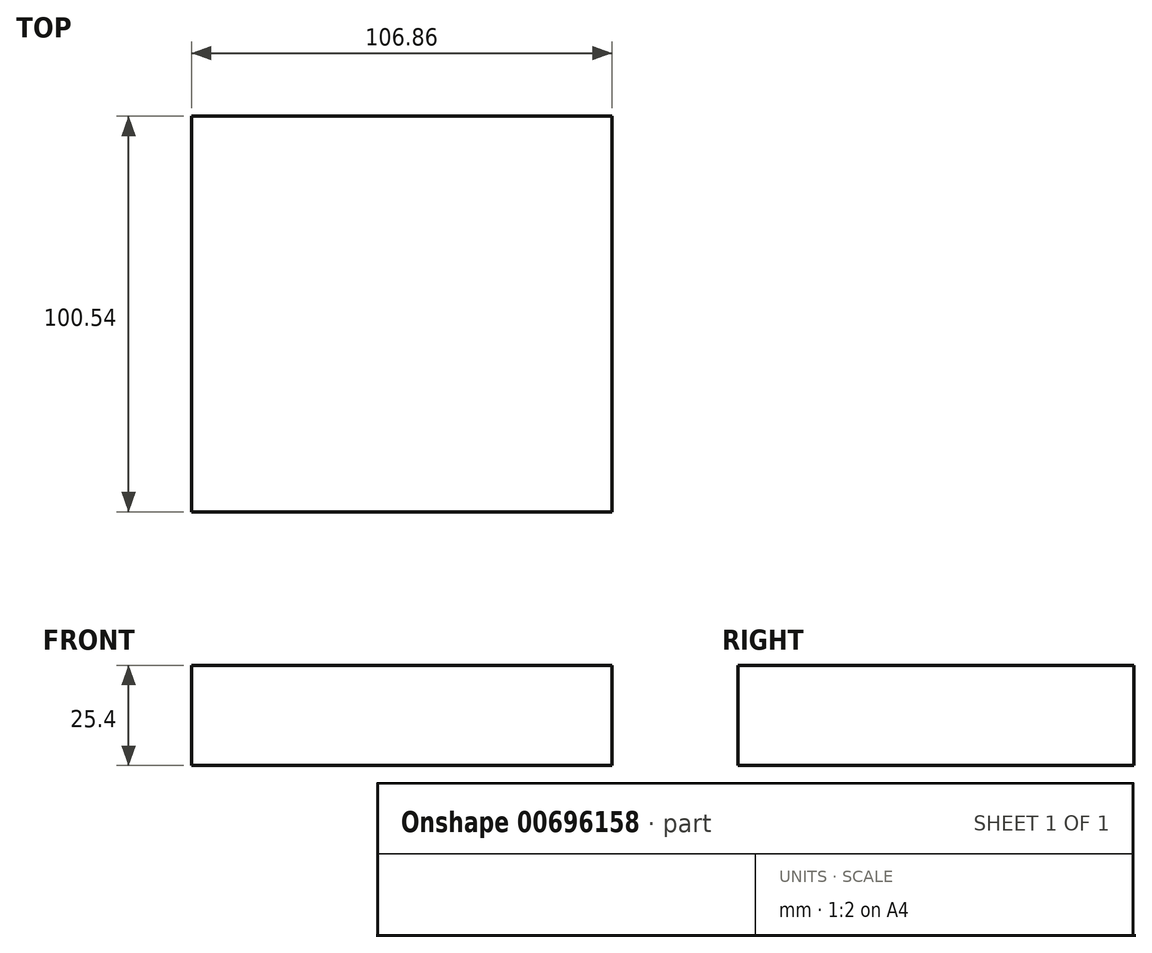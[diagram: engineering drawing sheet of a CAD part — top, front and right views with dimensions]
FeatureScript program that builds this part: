
annotation { "Feature Type Name" : "Feature", "Feature Type Description" : "" }
export const myFeature = defineFeature(function(context is Context, id is Id, definition is map)
    precondition{}
    {
        {
            var Q0;
            Q0=qCreatedBy(makeId("Top.planeOp"),FACE);
            var sketch = newSketch(context, id + "F0", { "sketchPlane" : qUnion([Q0])});
            skLineSegment(sketch, "E0.bottom", {"start": v(-51.68, 50.95) * mm, "end": v(55.18, 50.95) * mm});
            skLineSegment(sketch, "E0.top", {"start": v(-51.68, -49.6) * mm, "end": v(55.18, -49.6) * mm});
            skLineSegment(sketch, "E0.left", {"start": v(-51.68, 50.95) * mm, "end": v(-51.68, -49.6) * mm});
            skLineSegment(sketch, "E0.right", {"start": v(55.18, 50.95) * mm, "end": v(55.18, -49.6) * mm});
            skSolve(sketch);
        }
        {
            var Q0;
            Q0=makeQuery(id+"F0.imprint","IMPRINT",FACE,{"disambiguationData":[TD([[makeQuery(id+"F0.imprint","IMPRINT",EDGE,{"derivedFrom":sQuery(id+"F0.wireOp",EDGE,"E0.bottom")}),-1.0]])]});
            extrude(context, id + "F1", {"entities" : qUnion([Q0]), "depth" : 25.4 * mm, "offsetDistance" : 25.4 * mm});
        }
    });
